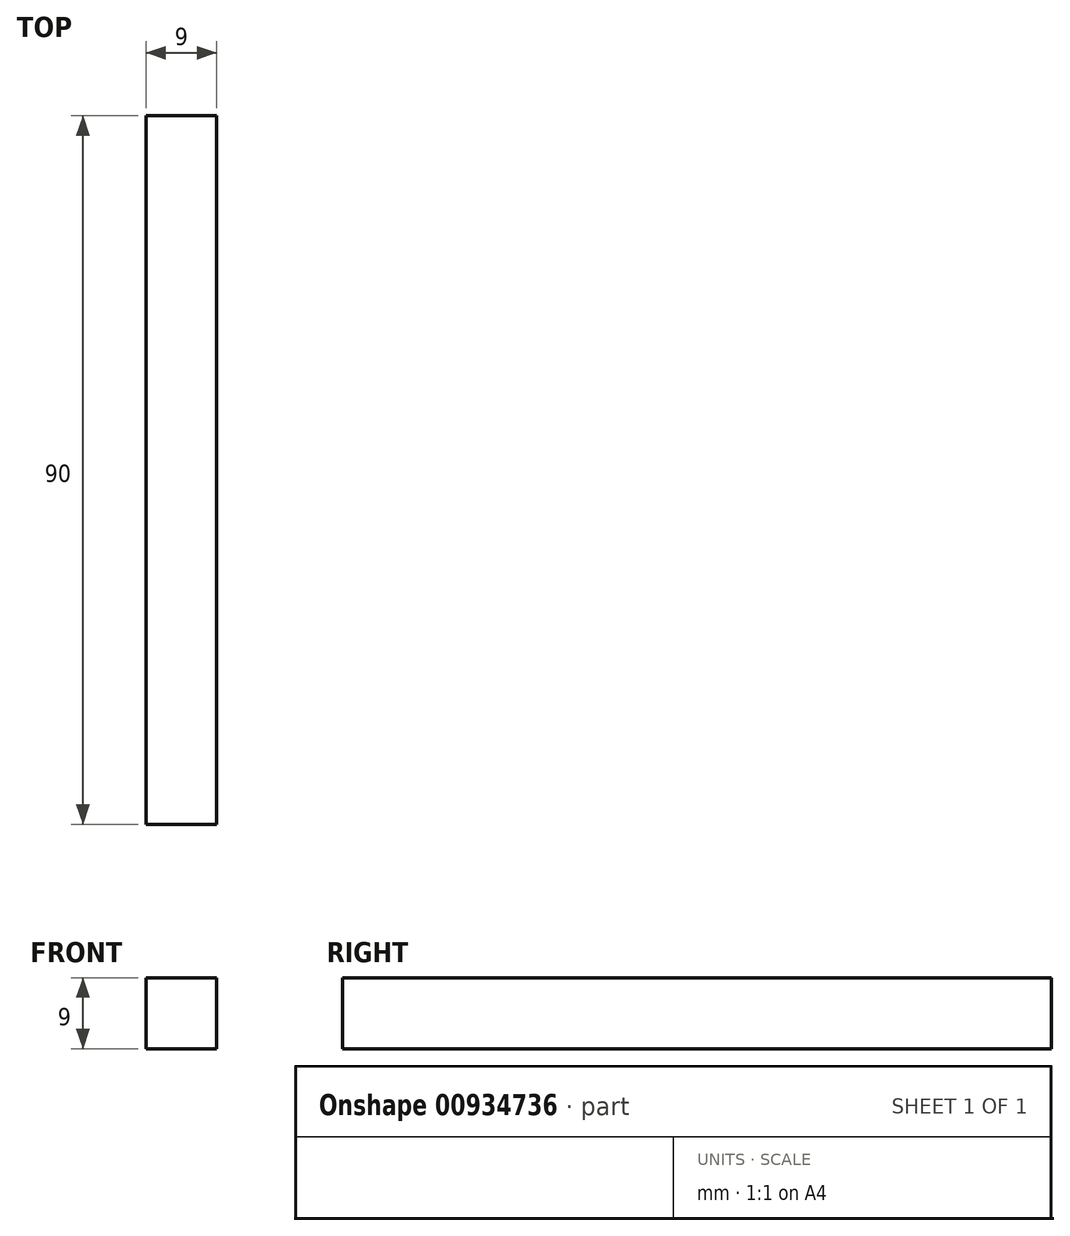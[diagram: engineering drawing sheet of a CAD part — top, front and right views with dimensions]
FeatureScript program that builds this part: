
annotation { "Feature Type Name" : "Feature", "Feature Type Description" : "" }
export const myFeature = defineFeature(function(context is Context, id is Id, definition is map)
    precondition{}
    {
        {
            var Q0;
            Q0=qCreatedBy(makeId("Front.planeOp"),FACE);
            var sketch = newSketch(context, id + "F0", { "sketchPlane" : qUnion([Q0])});
            skLineSegment(sketch, "E0.bottom", {"start": v(-4.5, 4.5) * mm, "end": v(4.5, 4.5) * mm});
            skLineSegment(sketch, "E0.top", {"start": v(-4.5, -4.5) * mm, "end": v(4.5, -4.5) * mm});
            skLineSegment(sketch, "E0.left", {"start": v(-4.5, 4.5) * mm, "end": v(-4.5, -4.5) * mm});
            skLineSegment(sketch, "E0.right", {"start": v(4.5, 4.5) * mm, "end": v(4.5, -4.5) * mm});
            skPoint(sketch, "E0.middle", {"position": v(0, 0) * mm});
            skSolve(sketch);
        }
        {
            var Q0;
            Q0=makeQuery(id+"F0.imprint","IMPRINT",FACE,{"disambiguationData":[TD([[makeQuery(id+"F0.imprint","IMPRINT",EDGE,{"derivedFrom":sQuery(id+"F0.wireOp",EDGE,"E0.bottom")}),-1.0]])]});
            extrude(context, id + "F1", {"entities" : qUnion([Q0]), "depth" : 90 * mm, "offsetDistance" : 25 * mm});
        }
    });
